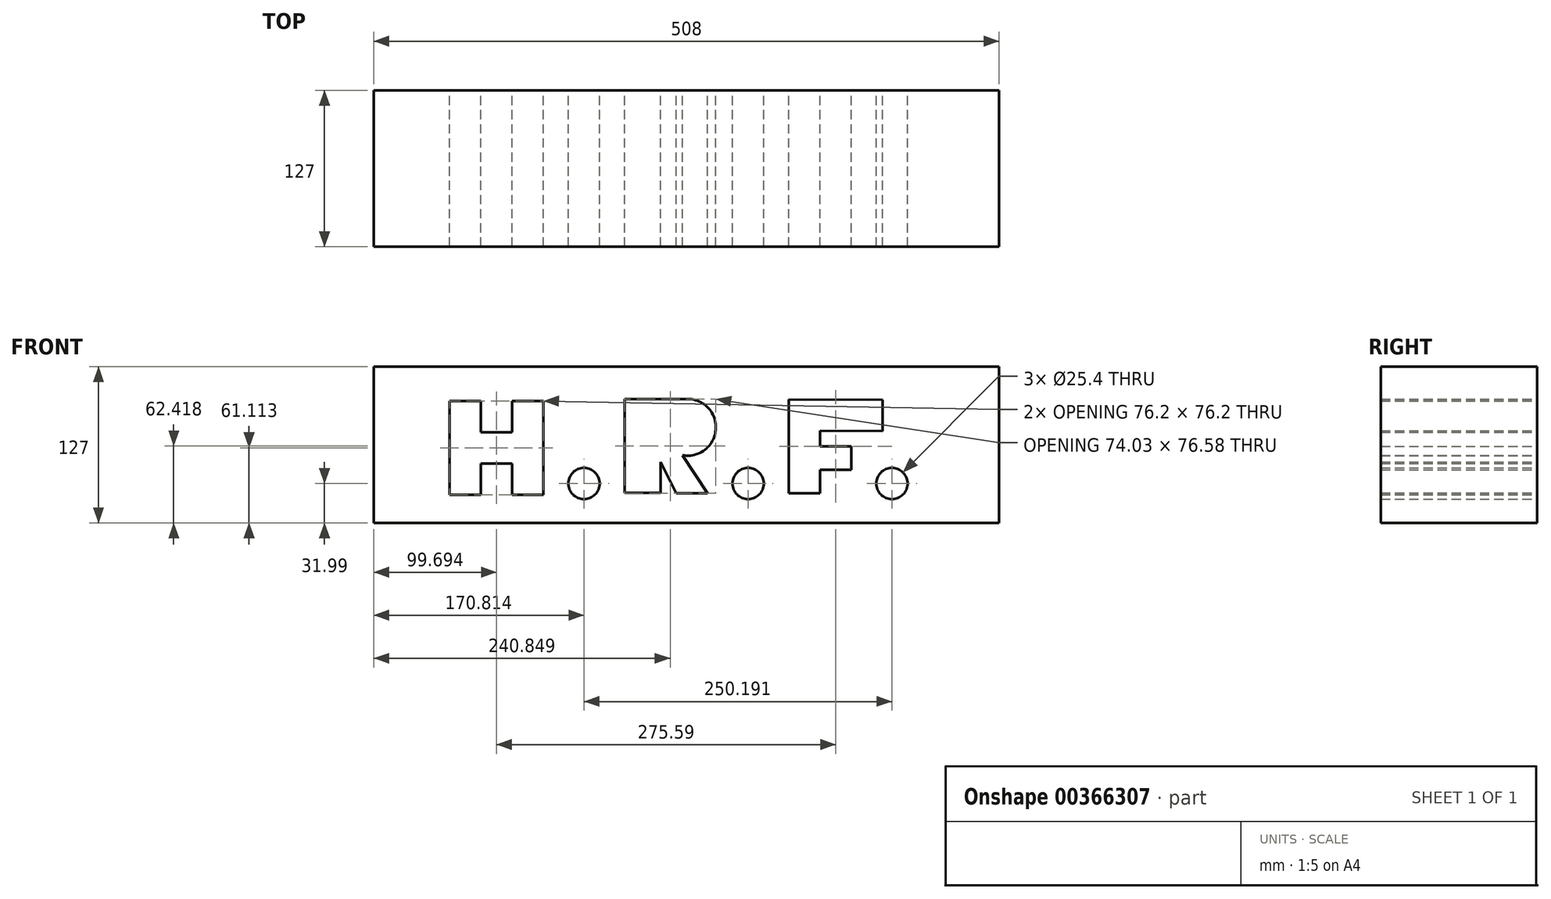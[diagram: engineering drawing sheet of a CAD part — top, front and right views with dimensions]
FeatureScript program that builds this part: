
annotation { "Feature Type Name" : "Feature", "Feature Type Description" : "" }
export const myFeature = defineFeature(function(context is Context, id is Id, definition is map)
    precondition{}
    {
        {
            var Q0;
            Q0=qCreatedBy(makeId("Front.planeOp"),FACE);
            var sketch = newSketch(context, id + "F0", { "sketchPlane" : qUnion([Q0])});
            skLineSegment(sketch, "E0", {"start": v(-616.03, 95) * mm, "end": v(-108.03, 95) * mm});
            skLineSegment(sketch, "E1", {"start": v(-108.03, 95) * mm, "end": v(-108.03, -32) * mm});
            skLineSegment(sketch, "E2", {"start": v(-108.03, -32) * mm, "end": v(-616.03, -32) * mm});
            skLineSegment(sketch, "E3", {"start": v(-616.03, -32) * mm, "end": v(-616.03, 95) * mm});
            skLineSegment(sketch, "E4", {"start": v(-529.04, 67.22) * mm, "end": v(-554.44, 67.22) * mm});
            skLineSegment(sketch, "E5", {"start": v(-554.44, 67.22) * mm, "end": v(-554.44, -8.98) * mm});
            skLineSegment(sketch, "E6", {"start": v(-554.44, -8.98) * mm, "end": v(-529.04, -8.98) * mm});
            skLineSegment(sketch, "E7", {"start": v(-529.04, -8.98) * mm, "end": v(-529.04, 16.42) * mm});
            skLineSegment(sketch, "E8", {"start": v(-529.04, 16.42) * mm, "end": v(-503.64, 16.42) * mm});
            skLineSegment(sketch, "E9", {"start": v(-503.64, 16.42) * mm, "end": v(-503.64, -8.98) * mm});
            skLineSegment(sketch, "E10", {"start": v(-503.64, -8.98) * mm, "end": v(-478.24, -8.98) * mm});
            skLineSegment(sketch, "E11", {"start": v(-478.24, -8.98) * mm, "end": v(-478.24, 67.22) * mm});
            skLineSegment(sketch, "E12", {"start": v(-478.24, 67.22) * mm, "end": v(-503.64, 67.22) * mm});
            skLineSegment(sketch, "E13", {"start": v(-503.64, 67.22) * mm, "end": v(-503.64, 41.82) * mm});
            skLineSegment(sketch, "E14", {"start": v(-503.64, 41.82) * mm, "end": v(-529.04, 41.82) * mm});
            skLineSegment(sketch, "E15", {"start": v(-529.04, 41.82) * mm, "end": v(-529.04, 67.22) * mm});
            skCircle(sketch, "E16", {"center": v(-445.22, 0) * mm, "radius": 12.7 * mm});
            skLineSegment(sketch, "E17", {"start": v(-412.2, 68.72) * mm, "end": v(-412.2, -7.4) * mm});
            skLineSegment(sketch, "E18", {"start": v(-412.2, -7.4) * mm, "end": v(-382.87, -7.4) * mm});
            skLineSegment(sketch, "E19", {"start": v(-382.87, -7.4) * mm, "end": v(-382.87, 17.54) * mm});
            skLineSegment(sketch, "E20", {"start": v(-412.2, 68.72) * mm, "end": v(-361.1, 68.72) * mm});
            skArc(sketch, "E21", {"start": v(-365.2, 23.01) * mm, "mid": v(-338.17, 43.63) * mm, "end": v(-361.1, 68.72) * mm});
            skLineSegment(sketch, "E22", {"start": v(-365.2, 23.01) * mm, "end": v(-344.88, -7.86) * mm});
            skLineSegment(sketch, "E23", {"start": v(-344.88, -7.86) * mm, "end": v(-370.28, -7.86) * mm});
            skLineSegment(sketch, "E24", {"start": v(-370.28, -7.86) * mm, "end": v(-382.87, 17.54) * mm});
            skCircle(sketch, "E25", {"center": v(-311.86, 0) * mm, "radius": 12.7 * mm});
            skLineSegment(sketch, "E26", {"start": v(-278.84, -7.86) * mm, "end": v(-278.84, 68.34) * mm});
            skLineSegment(sketch, "E27", {"start": v(-278.84, 68.34) * mm, "end": v(-202.65, 68) * mm});
            skLineSegment(sketch, "E28", {"start": v(-202.65, 68) * mm, "end": v(-202.65, 42.6) * mm});
            skLineSegment(sketch, "E29", {"start": v(-278.84, -7.86) * mm, "end": v(-253.44, -7.86) * mm});
            skLineSegment(sketch, "E30", {"start": v(-253.44, -7.86) * mm, "end": v(-253.44, 11.2) * mm});
            skLineSegment(sketch, "E31", {"start": v(-253.44, 11.2) * mm, "end": v(-228.04, 11.2) * mm});
            skLineSegment(sketch, "E32", {"start": v(-228.04, 11.2) * mm, "end": v(-228.04, 30.08) * mm});
            skLineSegment(sketch, "E33", {"start": v(-228.04, 30.08) * mm, "end": v(-253.45, 30.08) * mm});
            skLineSegment(sketch, "E34", {"start": v(-202.65, 42.6) * mm, "end": v(-253.45, 42.82) * mm});
            skLineSegment(sketch, "E35", {"start": v(-253.45, 42.82) * mm, "end": v(-253.45, 30.08) * mm});
            skCircle(sketch, "E36", {"center": v(-195.02, 0) * mm, "radius": 12.7 * mm});
            skSolve(sketch);
        }
        {
            var Q0;
            Q0=makeQuery(id+"F0.imprint","IMPRINT",FACE,{"disambiguationData":[TD([[makeQuery(id+"F0.imprint","IMPRINT",EDGE,{"derivedFrom":sQuery(id+"F0.wireOp",EDGE,"E0")}),-1.0]])]});
            extrude(context, id + "F1", {"entities" : qUnion([Q0]), "depth" : 127 * mm});
        }
    });
